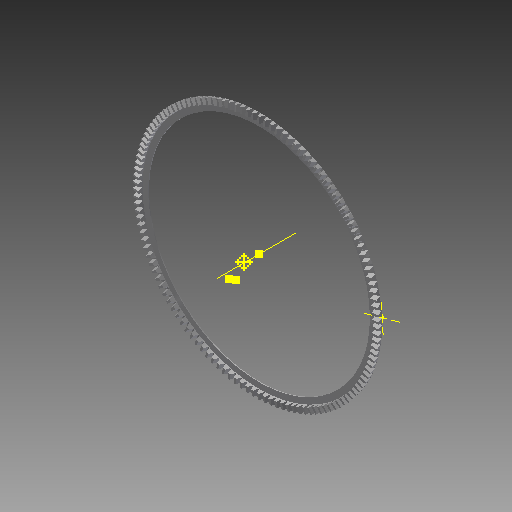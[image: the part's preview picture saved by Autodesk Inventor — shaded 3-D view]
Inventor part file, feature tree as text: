
AUTODESK INVENTOR PART (.ipt)
format: ipt  version: 2017 (Build 210142000, 142)  size: 1,788,416 bytes
history: native  units: mm
features: other x24, sketch x4, loft x2, pattern_circular x2, extrude x1
ambient origin geometry x6: Origin, XZ Plane, X Axis, Y Axis, Z Axis, Center Point
bodies: Solid1 (feature_tree)
feature tree (33):
  other  "Top Point"
  other  "Mesh Plane2"
  other  "Teeth Body"
  other  "Start Point"
  other  "Tooth Plane"
  other  "Start Sketch"
  other  "End Point"
  other  "3D Sketch Right"
  other  "End Plane Right"
  loft  "Loft Right"
  pattern_circular  "Circular Pattern Right"  Angle=90.0deg  [1 undecoded]
  other  "3D Sketch Left"
  other  "End Plane Left"
  loft  "Loft Left"
  pattern_circular  "Circular Pattern Left"  [2 undecoded]
  other  "Fix Body"
  sketch  "Sketch8"  dims[d2=325.711267mm]
  extrude  "Extrusion1"  Depth=10.0mm
  sketch  "Sketch10"  dims[d4=16.527263mm d5=90.0deg d7=478.580124mm d8=454.184503mm d9=1239.94227mm d11=7.8994mm d12=455.960761mm d15=432.718163mm d16=1181.338282mm d17=0.0mm d18=90.0deg d19=0.0mm d20=90.0deg d21=1280.0mm d22=360.0deg d26=314.208686mm d27=0.919419mm d28=325.12mm d29=-14.541409mm d30=455.960761mm d31=432.718163mm d32=1181.338282mm d35=0.0mm d37=0.0mm d39=0.0mm d40=90.0deg d41=1280.0mm d42=360.0deg d46=90.0deg d47=90.0deg d48=0.0mm d49=0.0mm d50=90.0deg d51=0.245437mm d52=0.0mm d53=0.0mm d54=0.0mm d56=18.102912mm d57=1400.887588mm d58=1392.952628mm d59=1334.676764mm d60=1327.116838mm d61=1334.676764mm d62=1327.116838mm d63=90.0deg d64=90.0deg d65=314.208686mm d66=31.5mm d67=325.12mm d68=-14.541409mm d69=0.919419mm d70=432.718163mm d71=1181.338282mm d72=455.960761mm d73=1327.116838mm d74=1334.676764mm d75=0.0mm d76=90.0deg d77=0.0mm d78=90.0deg d79=0.0mm d80=90.0deg d81=1280.0mm d82=360.0deg d84=10.0mm d85=20.0mm d86=20.0mm d87=10.0mm d88=0.0mm d89=0.0mm d90=25.4mm d91=0.0mm]
  other  "Mesh Plane"
  other  "Top Plane"
  other  "Teeth Body Sketch"
  other  "End Plane"
  other  "End Sketch"
  other  "Helical Curve Left"
  other  "End Sketch Left"
  other  "Body Sketch"
  sketch  "Sketch6"  dims[d0=325.12mm d1=324.41048mm]
  other  "Srf1"
  other  "Helical Curve Right"
  other  "End Sketch Right"
  sketch  "Sketch9"  dims[d3=7.62mm]
  other  "Pitch Diameter"
note: 3 required parameter values undecoded (feature->parameter linkage not recoverable at this tier; creation-order binding heuristic only, values carry confidence <= 0.55)
